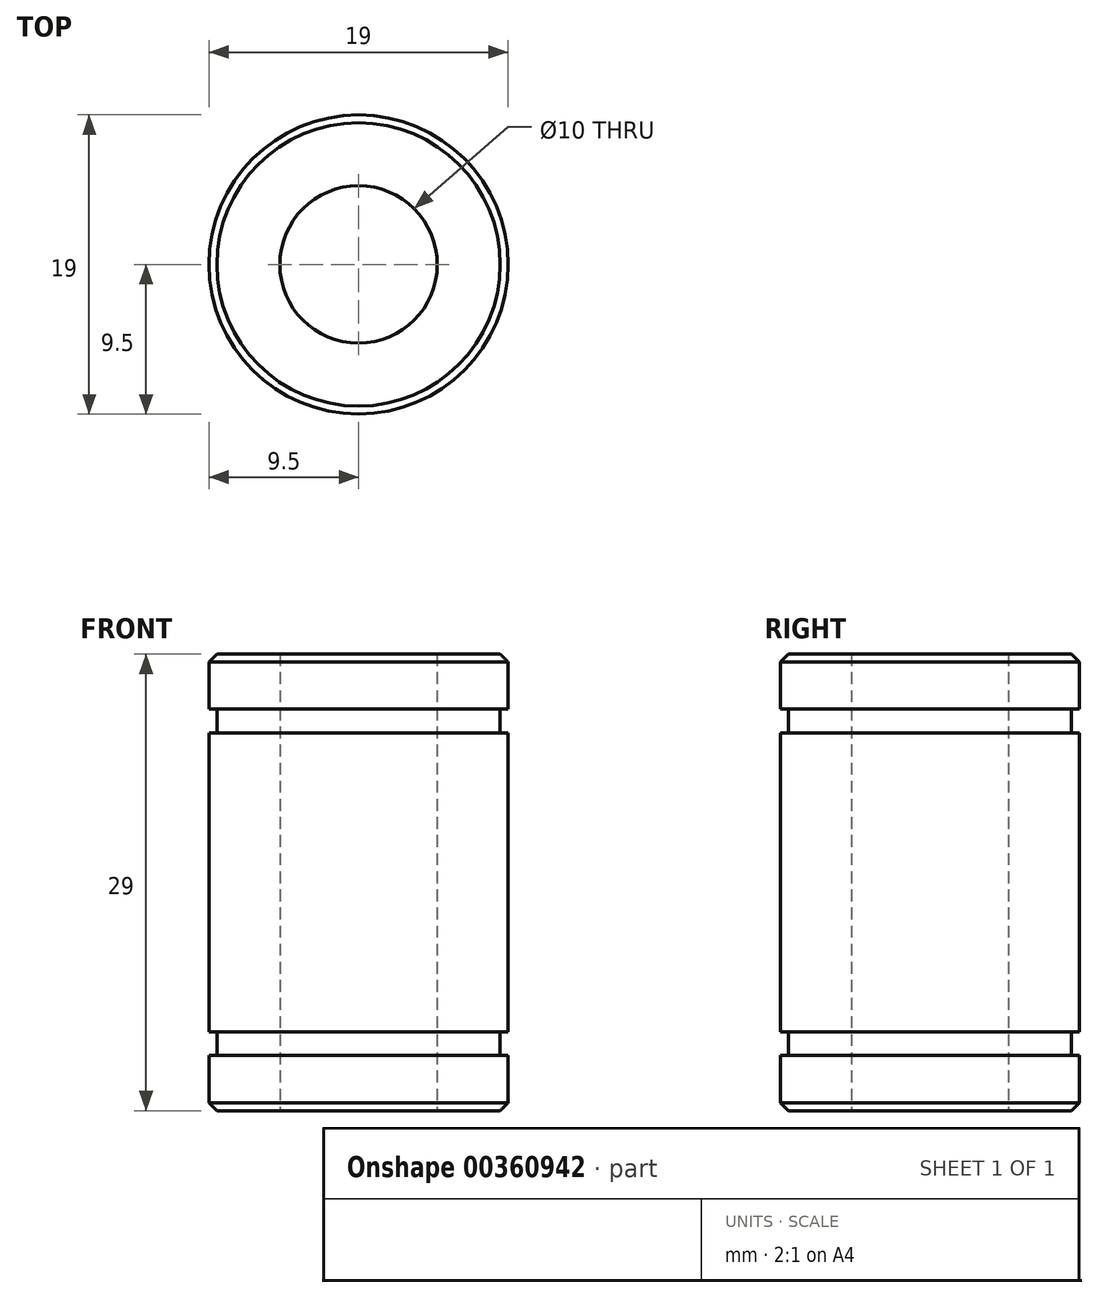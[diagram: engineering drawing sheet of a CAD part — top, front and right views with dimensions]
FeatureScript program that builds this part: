
annotation { "Feature Type Name" : "Feature", "Feature Type Description" : "" }
export const myFeature = defineFeature(function(context is Context, id is Id, definition is map)
    precondition{}
    {
        {
            var Q0;
            Q0=qCreatedBy(makeId("Top.planeOp"),FACE);
            var sketch = newSketch(context, id + "F0", { "sketchPlane" : qUnion([Q0])});
            skCircle(sketch, "E0", {"center": v(0, 0) * mm, "radius": 9.5 * mm});
            skCircle(sketch, "E1", {"center": v(0, 0) * mm, "radius": 5 * mm});
            skSolve(sketch);
        }
        {
            var Q0;
            Q0=qSketchRegion(id+"F0",true);
            extrude(context, id + "F1", {"entities" : qUnion([Q0]), "depth" : 29 * mm});
        }
        {
            var Q0;
            Q0=makeQuery(id+"F1.opExtrude","CAP_EDGE",EDGE,{"disambiguationData":[OSD([sQuery(id+"F0.wireOp",EDGE,"E0")])],"isStart":false});
            var Q1;
            Q1=makeQuery(id+"F1.opExtrude","CAP_EDGE",EDGE,{"disambiguationData":[OSD([sQuery(id+"F0.wireOp",EDGE,"E0")])],"isStart":true});
            chamfer(context, id + "F2", {"entities" : qUnion([Q0, Q1]), "width" : 0.5 * mm, "tangentPropagation" : true});
        }
        {
            var Q0;
            Q0=makeQuery(id+"F1.opExtrude","CAP_FACE",FACE,{"disambiguationData":[OSD([sQuery(id+"F0.wireOp",EDGE,"E0"),sQuery(id+"F0.wireOp",EDGE,"E1")])],"isStart":true});
            cPlane(context, id + "F3", {"entities" : qUnion([Q0]), "cplaneType" : CPlaneType.OFFSET, "offset" : 3.5 * mm, "oppositeDirection" : true, "width" : 150 * mm, "height" : 150 * mm});
        }
        {
            var Q0;
            Q0=qCreatedBy(id+"F3.planeOp",FACE);
            var sketch = newSketch(context, id + "F4", { "sketchPlane" : qUnion([Q0])});
            skCircle(sketch, "E2", {"center": v(0, 0) * mm, "radius": 9.5 * mm});
            skCircle(sketch, "E3", {"center": v(0, 0) * mm, "radius": 9 * mm});
            skSolve(sketch);
        }
        {
            var Q0;
            Q0=qSketchRegion(id+"F4",true);
            extrude(context, id + "F5", {"entities" : qUnion([Q0]), "operationType" : NewBodyOperationType.REMOVE, "oppositeDirection" : true, "depth" : 1.5 * mm});
        }
        {
            var Q0;
            Q0=makeQuery(id+"F1.opExtrude","CAP_FACE",FACE,{"disambiguationData":[OSD([sQuery(id+"F0.wireOp",EDGE,"E0"),sQuery(id+"F0.wireOp",EDGE,"E1")])],"isStart":false});
            cPlane(context, id + "F6", {"entities" : qUnion([Q0]), "cplaneType" : CPlaneType.OFFSET, "offset" : 3.5 * mm, "oppositeDirection" : true, "width" : 150 * mm, "height" : 150 * mm});
        }
        {
            var Q0;
            Q0=qCreatedBy(id+"F6.planeOp",FACE);
            var sketch = newSketch(context, id + "F7", { "sketchPlane" : qUnion([Q0])});
            skCircle(sketch, "E4", {"center": v(0, 0) * mm, "radius": 9 * mm});
            skCircle(sketch, "E5", {"center": v(0, 0) * mm, "radius": 9.5 * mm});
            skSolve(sketch);
        }
        {
            var Q0;
            Q0=qSketchRegion(id+"F7",true);
            extrude(context, id + "F8", {"entities" : qUnion([Q0]), "operationType" : NewBodyOperationType.REMOVE, "oppositeDirection" : true, "depth" : 1.5 * mm});
        }
    });
